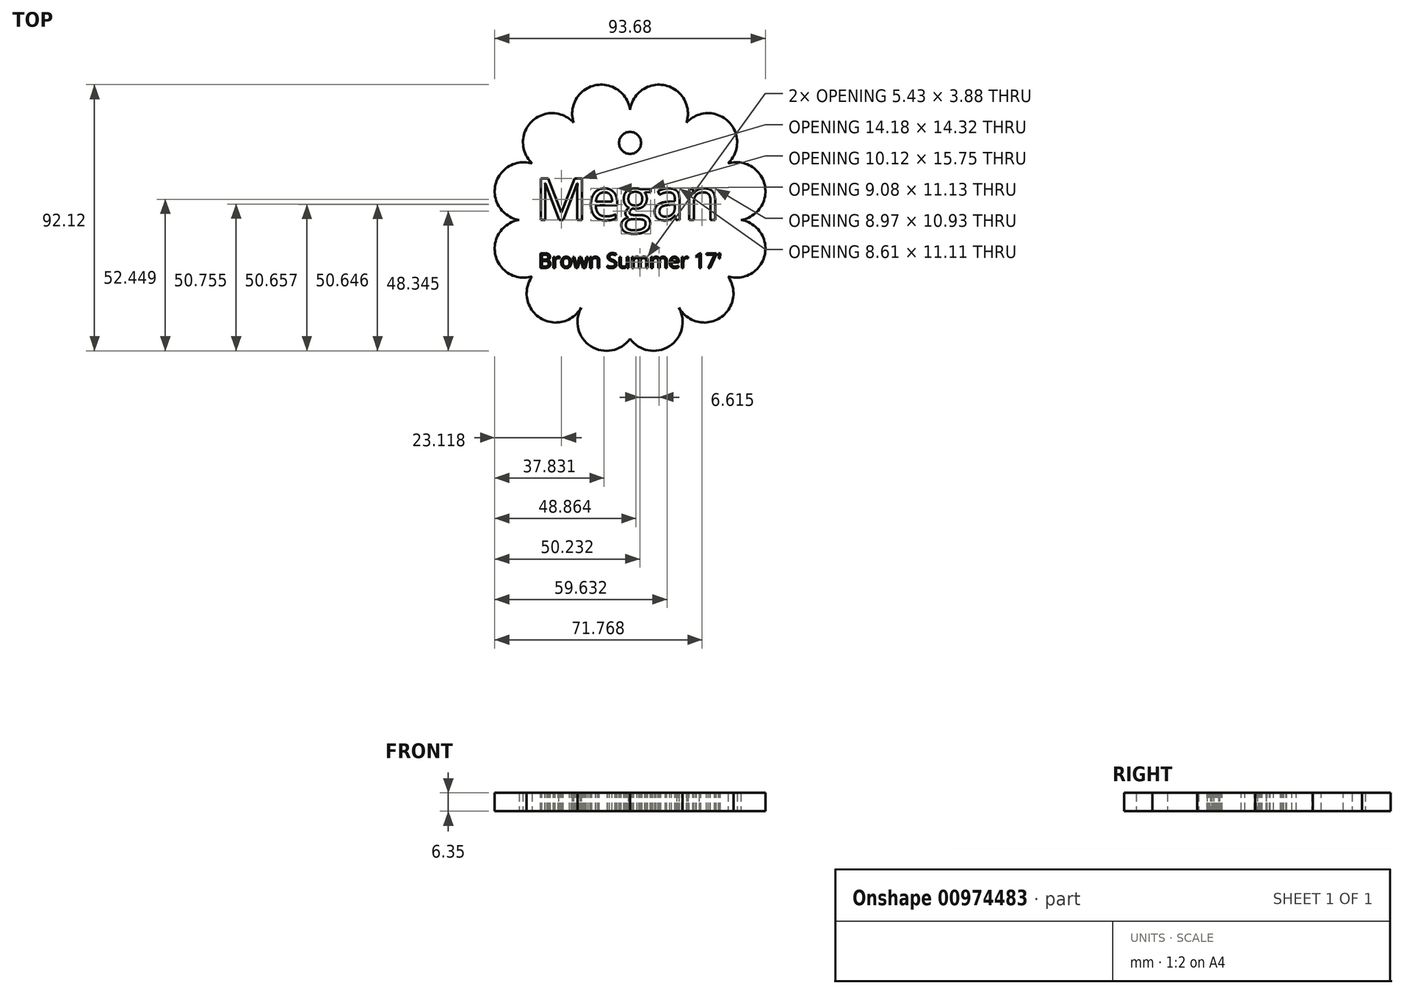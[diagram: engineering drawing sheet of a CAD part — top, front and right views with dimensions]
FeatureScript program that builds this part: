
annotation { "Feature Type Name" : "Feature", "Feature Type Description" : "" }
export const myFeature = defineFeature(function(context is Context, id is Id, definition is map)
    precondition{}
    {
        {
            var Q0;
            Q0=qCreatedBy(makeId("Top.planeOp"),FACE);
            var sketch = newSketch(context, id + "F0", { "sketchPlane" : qUnion([Q0])});
            skLineSegment(sketch, "E0", {"start": v(0, 38.1) * mm, "end": v(0, -41.13) * mm, "construction": true});
            skLineSegment(sketch, "E1", {"start": v(-33.85, 19.55) * mm, "end": v(0, 0) * mm, "construction": true});
            skLineSegment(sketch, "E2", {"start": v(0, 0) * mm, "end": v(-33.85, -19.55) * mm, "construction": true});
            skLineSegment(sketch, "E3", {"start": v(0, 0) * mm, "end": v(-16.93, -30.34) * mm, "construction": true});
            skPoint(sketch, "E3.endSnap0", {"position": v(-16.93, -9.77) * mm});
            skLineSegment(sketch, "E4", {"start": v(0, 0) * mm, "end": v(-17.44, 30.05) * mm, "construction": true});
            skLineSegment(sketch, "E5", {"start": v(0, 0) * mm, "end": v(-35.18, 0) * mm, "construction": true});
            skArc(sketch, "E6", {"start": v(0, 38.1) * mm, "mid": v(-14.18, 45.9) * mm, "end": v(-17.44, 30.05) * mm});
            skArc(sketch, "E7", {"start": v(-17.44, 30.05) * mm, "mid": v(-32.4, 35.36) * mm, "end": v(-33.85, 19.55) * mm});
            skArc(sketch, "E8", {"start": v(-33.85, 19.55) * mm, "mid": v(-46.82, 10.6) * mm, "end": v(-35.18, 0) * mm});
            skArc(sketch, "E9", {"start": v(-35.18, 0) * mm, "mid": v(-46.82, -10.6) * mm, "end": v(-33.85, -19.55) * mm});
            skArc(sketch, "E10", {"start": v(-33.85, -19.55) * mm, "mid": v(-31.11, -33.92) * mm, "end": v(-16.93, -30.34) * mm});
            skArc(sketch, "E11", {"start": v(-16.93, -30.34) * mm, "mid": v(-13.55, -43.72) * mm, "end": v(0, -41.13) * mm});
            skArc(sketch, "E12.MirrorCS", {"start": v(0, 38.1) * mm, "mid": v(14.18, 45.9) * mm, "end": v(17.44, 30.05) * mm});
            skArc(sketch, "E13.MirrorCS", {"start": v(17.44, 30.05) * mm, "mid": v(32.4, 35.36) * mm, "end": v(33.85, 19.55) * mm});
            skArc(sketch, "E14.MirrorCS", {"start": v(33.85, 19.55) * mm, "mid": v(46.82, 10.6) * mm, "end": v(35.18, 0) * mm});
            skArc(sketch, "E15.MirrorCS", {"start": v(35.18, 0) * mm, "mid": v(46.82, -10.6) * mm, "end": v(33.85, -19.55) * mm});
            skArc(sketch, "E16.MirrorCS", {"start": v(33.85, -19.55) * mm, "mid": v(31.11, -33.92) * mm, "end": v(16.93, -30.34) * mm});
            skArc(sketch, "E17.MirrorCS", {"start": v(16.93, -30.34) * mm, "mid": v(13.55, -43.72) * mm, "end": v(0, -41.13) * mm});
            skCircle(sketch, "E18", {"center": v(0, 0) * mm, "radius": 38.1 * mm, "construction": true});
            skSolve(sketch);
        }
        {
            var Q0;
            Q0 = qSketchRegion(id + "F0", true);
            extrude(context, id + "F1", {"entities" : qUnion([Q0]), "depth" : 6.35 * mm, "offsetDistance" : 25.4 * mm});
        }
        {
            var Q0;
            Q0=makeQuery(id+"F1.opExtrude","CAP_FACE",FACE,{"disambiguationData":[OSD([sQuery(id+"F0.wireOp",EDGE,"E6"),sQuery(id+"F0.wireOp",EDGE,"E7"),sQuery(id+"F0.wireOp",EDGE,"E8"),sQuery(id+"F0.wireOp",EDGE,"E9"),sQuery(id+"F0.wireOp",EDGE,"E10"),sQuery(id+"F0.wireOp",EDGE,"E11"),sQuery(id+"F0.wireOp",EDGE,"E12.MirrorCS"),sQuery(id+"F0.wireOp",EDGE,"E13.MirrorCS"),sQuery(id+"F0.wireOp",EDGE,"E14.MirrorCS"),sQuery(id+"F0.wireOp",EDGE,"E15.MirrorCS"),sQuery(id+"F0.wireOp",EDGE,"E16.MirrorCS"),sQuery(id+"F0.wireOp",EDGE,"E17.MirrorCS")])],"isStart":false});
            var sketch = newSketch(context, id + "F2", { "sketchPlane" : qUnion([Q0])});
            skText(sketch, "E19", { "text": "Megan\n", "fontName": "OpenSans-Regular.ttf"});
            const initialGuessF2  = {"E19": [-0.03278, 0, 1, 0, 0.01444]};
            skSetInitialGuess(sketch, initialGuessF2);
            skSolve(sketch);
        }
        {
            var Q0;
            Q0 = qSketchRegion(id + "F2", true);
            extrude(context, id + "F3", {"entities" : qUnion([Q0]), "operationType" : NewBodyOperationType.REMOVE, "oppositeDirection" : true, "depth" : 50.8 * mm, "offsetDistance" : 25.4 * mm});
        }
        {
            var Q0;
            {var subQ0=sQuery(id+"F0.wireOp",EDGE,"E17.MirrorCS");var subQ1=sQuery(id+"F0.wireOp",EDGE,"E16.MirrorCS");var subQ2=sQuery(id+"F0.wireOp",EDGE,"E8");var subQ3=sQuery(id+"F0.wireOp",EDGE,"E7");var subQ4=sQuery(id+"F0.wireOp",EDGE,"E9");var subQ5=sQuery(id+"F0.wireOp",EDGE,"E6");var subQ6=sQuery(id+"F0.wireOp",EDGE,"E15.MirrorCS");var subQ7=sQuery(id+"F0.wireOp",EDGE,"E10");var subQ8=sQuery(id+"F0.wireOp",EDGE,"E11");var subQ9=sQuery(id+"F0.wireOp",EDGE,"E12.MirrorCS");var subQ10=sQuery(id+"F0.wireOp",EDGE,"E13.MirrorCS");var subQ11=sQuery(id+"F0.wireOp",EDGE,"E14.MirrorCS");Q0=makeQuery(id+"F3.boolean.opBoolean","SPLIT",FACE,{"disambiguationData":[TD([makeQuery(id+"F1.opExtrude","SWEPT_FACE",FACE,{"disambiguationData":[OSD([subQ5])]})])],"derivedFrom":makeQuery(id+"F1.opExtrude","CAP_FACE",FACE,{"disambiguationData":[OSD([subQ5,subQ3,subQ2,subQ4,subQ7,subQ8,subQ9,subQ10,subQ11,subQ6,subQ1,subQ0])],"isStart":false})});}
            var sketch = newSketch(context, id + "F4", { "sketchPlane" : qUnion([Q0])});
            skText(sketch, "E20", { "text": "Brown Summer 17\' \n", "fontName": "OpenSans-Regular.ttf"});
            const initialGuessF4  = {"E20": [-0.03175, -0.01659, 1, 0, 0.00512]};
            skSetInitialGuess(sketch, initialGuessF4);
            skSolve(sketch);
        }
        {
            var Q0;
            Q0 = qSketchRegion(id + "F4", true);
            extrude(context, id + "F5", {"entities" : qUnion([Q0]), "operationType" : NewBodyOperationType.REMOVE, "oppositeDirection" : true, "depth" : 25.4 * mm, "offsetDistance" : 25.4 * mm});
        }
        {
            var Q0;
            {var subQ61=sQuery(id+"F0.wireOp",EDGE,"E6");var subQ62=makeQuery(id+"F1.opExtrude","SWEPT_FACE",FACE,{"disambiguationData":[OSD([subQ61])]});var subQ63=sQuery(id+"F0.wireOp",EDGE,"E9");var subQ65=sQuery(id+"F0.wireOp",EDGE,"E7");var subQ67=sQuery(id+"F0.wireOp",EDGE,"E8");var subQ69=sQuery(id+"F0.wireOp",EDGE,"E10");var subQ72=sQuery(id+"F0.wireOp",EDGE,"E11");var subQ75=sQuery(id+"F0.wireOp",EDGE,"E12.MirrorCS");var subQ78=sQuery(id+"F0.wireOp",EDGE,"E14.MirrorCS");var subQ81=sQuery(id+"F0.wireOp",EDGE,"E13.MirrorCS");var subQ84=sQuery(id+"F0.wireOp",EDGE,"E15.MirrorCS");var subQ88=sQuery(id+"F0.wireOp",EDGE,"E16.MirrorCS");var subQ92=sQuery(id+"F0.wireOp",EDGE,"E17.MirrorCS");Q0=makeQuery(id+"F5.boolean.opBoolean","SPLIT",FACE,{"disambiguationData":[TD([subQ62])],"derivedFrom":makeQuery(id+"F3.boolean.opBoolean","SPLIT",FACE,{"disambiguationData":[TD([subQ62])],"derivedFrom":makeQuery(id+"F1.opExtrude","CAP_FACE",FACE,{"disambiguationData":[OSD([subQ61,subQ65,subQ67,subQ63,subQ69,subQ72,subQ75,subQ81,subQ78,subQ84,subQ88,subQ92])],"isStart":false})})});}
            var sketch = newSketch(context, id + "F6", { "sketchPlane" : qUnion([Q0])});
            skCircle(sketch, "E21", {"center": v(0, 26.67) * mm, "radius": 3.81 * mm});
            skLineSegment(sketch, "E22", {"start": v(0, 26.67) * mm, "end": v(0, 0) * mm, "construction": true});
            skSolve(sketch);
        }
        {
            var Q0;
            Q0 = qSketchRegion(id + "F6", true);
            extrude(context, id + "F7", {"entities" : qUnion([Q0]), "operationType" : NewBodyOperationType.REMOVE, "oppositeDirection" : true, "depth" : 25.4 * mm, "offsetDistance" : 25.4 * mm});
        }
    });
